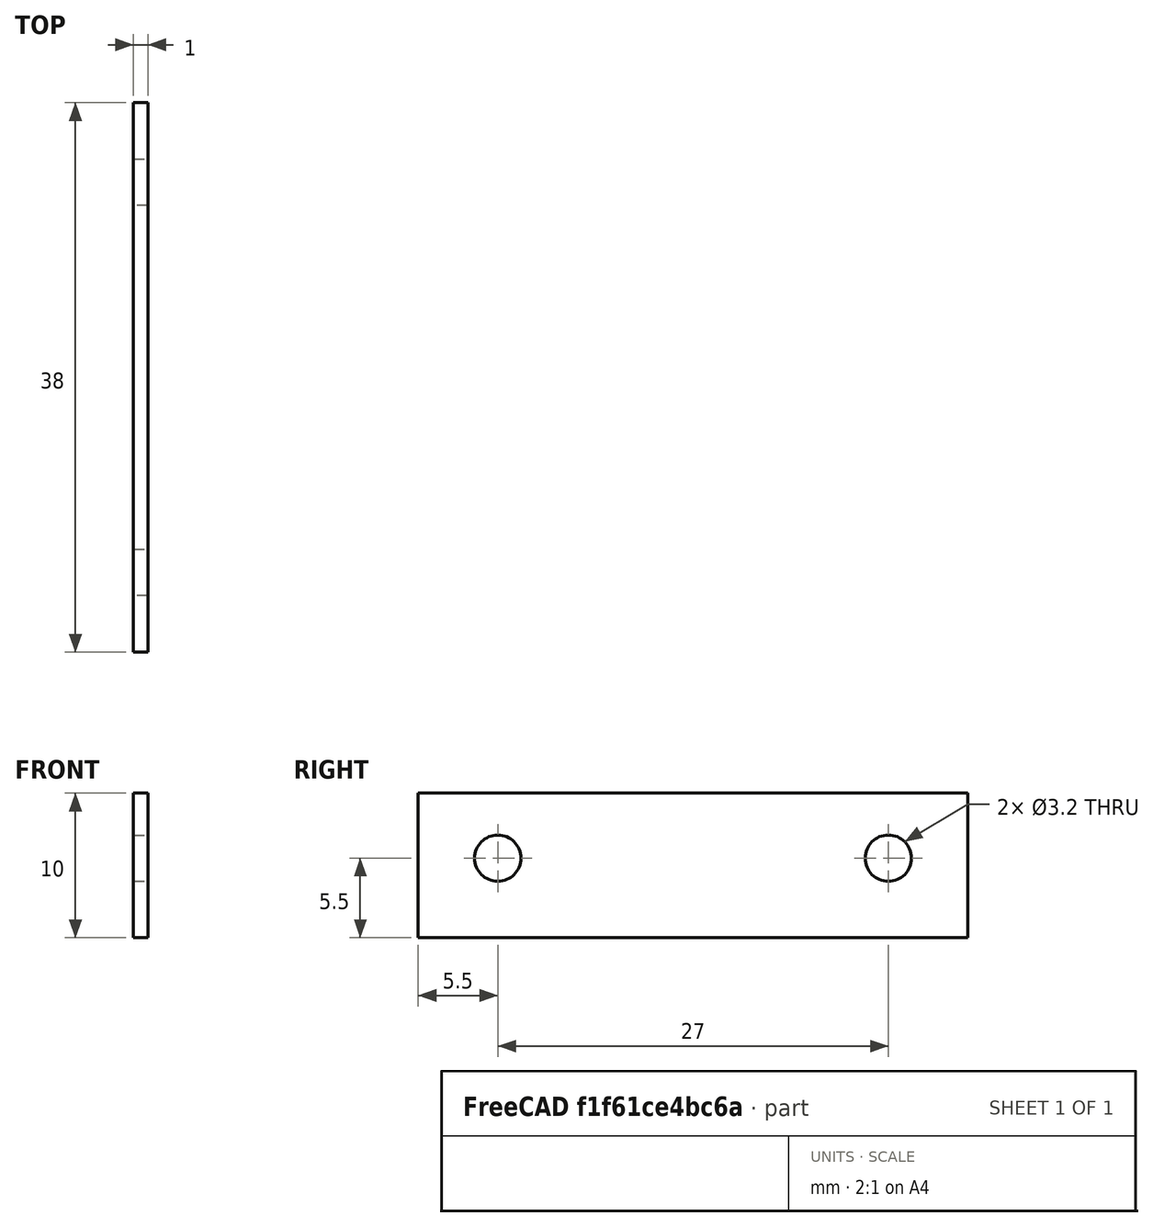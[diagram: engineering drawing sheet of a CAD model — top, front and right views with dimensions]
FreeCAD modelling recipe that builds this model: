
FCSTD DOCUMENT  (FreeCAD 0.16R)
Label: SeparadorAjuste_Motor
License: All rights reserved
LicenseURL: http://en.wikipedia.org/wiki/All_rights_reserved
objects: Sketcher::SketchObject×1, PartDesign::Pad×1
note: 3 computed .brp shape members not serialized (recipe doc carries the construction recipe); baked Part::Feature solids carry a one-line shape summary decoded from their .brp

FEATURE [Sketcher::SketchObject] Sketch002
  Placement = pos=(0,0,0) rot=(0.57735,-0.57735,-0.57735;2.0944rad)
  sketch-geometry (6):
    g0: Circle CenterX=-5.5 CenterY=5.5 CenterZ=0 NormalX=0 NormalY=0 NormalZ=1 Radius=1.6
    g1: Circle CenterX=-32.5 CenterY=5.5 CenterZ=0 NormalX=0 NormalY=0 NormalZ=1 Radius=1.6
    g2: LineSegment StartX=-38 StartY=10 StartZ=0 EndX=0 EndY=10 EndZ=0
    g3: LineSegment StartX=0 StartY=10 StartZ=0 EndX=0 EndY=0 EndZ=0
    g4: LineSegment StartX=0 StartY=0 StartZ=0 EndX=-38 EndY=0 EndZ=0
    g5: LineSegment StartX=-38 StartY=0 StartZ=0 EndX=-38 EndY=10 EndZ=0
  constraints (17):
    c: Radius(g0) = 1.6
    c: Equal(g1,g0)
    c: DistanceX(g1,g0) = 27
    c: DistanceY(g0,g1) = 0
    c: DistanceX(g0,g-1) = 5.5
    c: DistanceY(g-1,g0) = 5.5
    c: Coincident(g2,g3)
    c: Coincident(g3,g4)
    c: Coincident(g4,g5)
    c: Coincident(g5,g2)
    c: Horizontal(g2)
    c: Horizontal(g4)
    c: Vertical(g3)
    c: Vertical(g5)
    c: Coincident(g3,g-1)
    c: DistanceX(g2,g2) = 38
    c: DistanceY(g5,g5) = 10
FEATURE [PartDesign::Pad] Pad
  Length = 1
  Length2 = 100
  Placement = pos=(0,0,0) rot=(0.57735,-0.57735,-0.57735;2.0944rad)
  Sketch = -> Sketch002
  Type = 0
